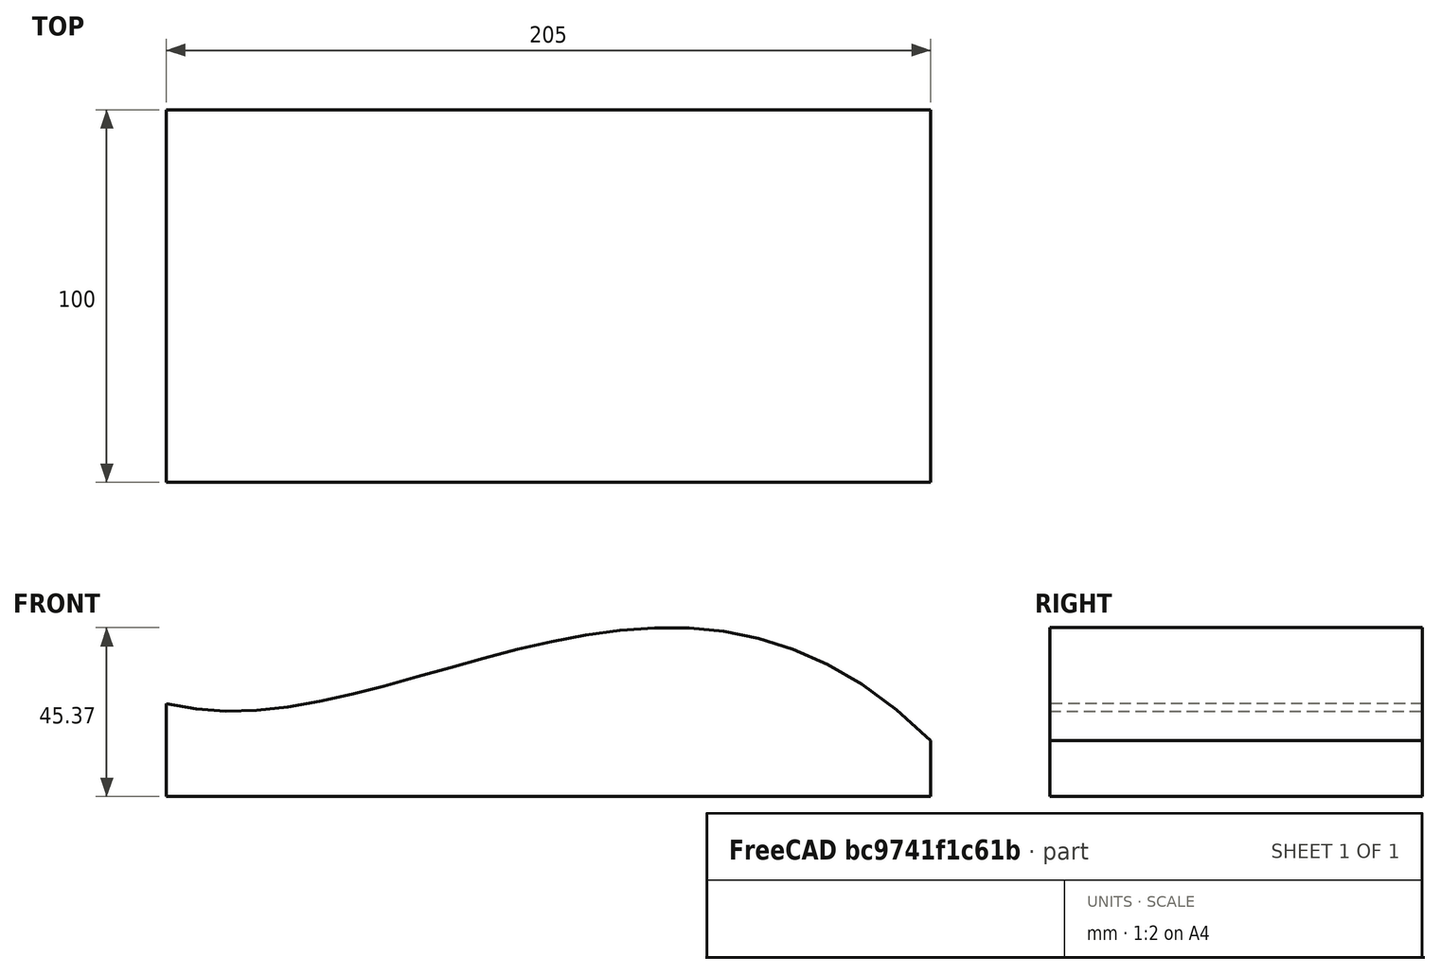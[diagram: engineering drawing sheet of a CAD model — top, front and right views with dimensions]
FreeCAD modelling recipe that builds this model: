
FCSTD DOCUMENT  (FreeCAD 0.19R16203 (Git))
Label: SplineSurface
License: All rights reserved
LicenseURL: http://en.wikipedia.org/wiki/All_rights_reserved
objects: Sketcher::SketchObject×1, PartDesign::Pad×1, PartDesign::Body×1
note: 4 computed .brp shape members not serialized (recipe doc carries the construction recipe); baked Part::Feature solids carry a one-line shape summary decoded from their .brp

FEATURE [Sketcher::SketchObject] Sketch
  MapMode = 5
  Placement = pos=(0,0,0) rot=(1,0,0;1.5708rad)
  Support = -> [XZ_Plane]
  sketch-geometry (10):
    g0-g3: Circle [constr] x4 (B-spline internal-alignment scaffolding for g4; pole/knot coordinates omitted)
    g4: BSplineCurve PolesCount=4 KnotsCount=2 Degree=3 IsPeriodic=0
    g5: GeomPoint [constr] X=-105 Y=25 Z=0
    g6: GeomPoint [constr] X=100 Y=15 Z=0
    g7: LineSegment StartX=-105 StartY=25 StartZ=0 EndX=-105 EndY=0 EndZ=0
    g8: LineSegment StartX=-105 StartY=0 StartZ=0 EndX=100 EndY=0 EndZ=0
    g9: LineSegment StartX=100 StartY=0 StartZ=0 EndX=100 EndY=15 EndZ=0
  constraints (23):
    c: Radius(g0) = 7
    c: Equal(g0,g1)
    c: Equal(g0,g2)
    c: Equal(g0,g3)
    c: InternalAlignment(g0-g3 -> g4) x4
    c: InternalAlignment(g5,g4)
    c: InternalAlignment(g6,g4)
    c: Coincident(g7,g4)
    c: PointOnObject(g8,g-1)
    c: Horizontal(g8)
    c: Coincident(g8,g9)
    c: Coincident(g9,g4)
    c: Vertical(g9)
    c: Coincident(g7,g8)
    c: DistanceY(g7,g7) = 25
    c: DistanceY(g9,g9) = 15
    c: Vertical(g7)
    c: DistanceX(g1,g2) = 75
    c: DistanceY(g1,g2) = 75
    c: DistanceX(g7,g1) = 60
    c: DistanceY(g7,g1) = 10
    c: DistanceX(g2,g4) = 70
    c: DistanceX(g8) = 100
FEATURE [PartDesign::Pad] Pad
  Length = 100
  Length2 = 100
  Placement = pos=(0,0,0) rot=(1,0,0;1.5708rad)
  Profile = -> Sketch
  Type = 0
FEATURE [PartDesign::Body] Body
  Group = -> [Sketch,Pad]
  Origin = -> Origin
  Tip = -> Pad
